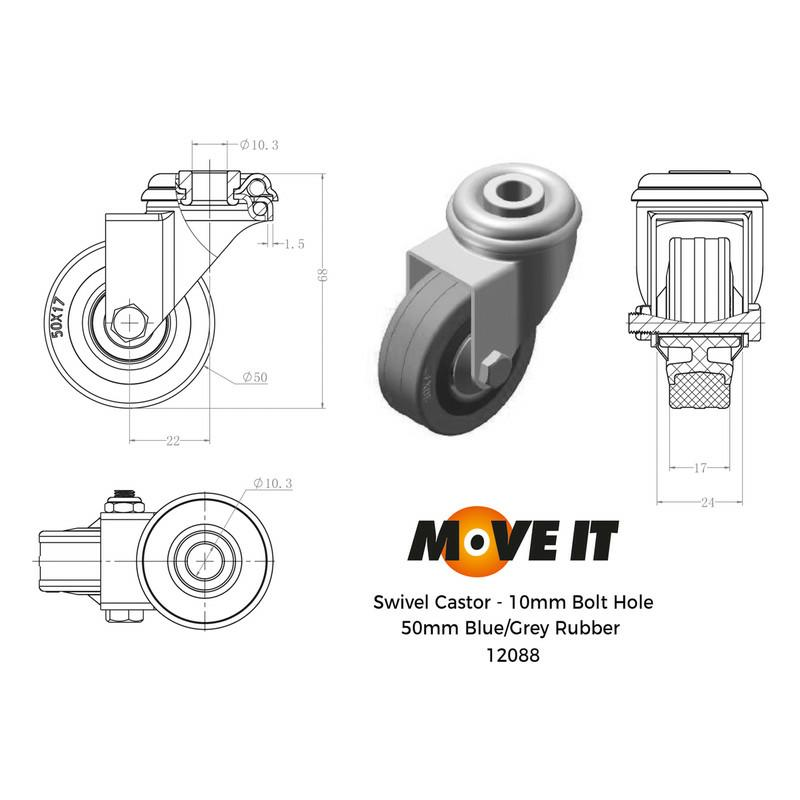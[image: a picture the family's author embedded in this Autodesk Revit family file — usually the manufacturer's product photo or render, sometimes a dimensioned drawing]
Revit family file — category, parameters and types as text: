
# Revit family: ThinkingWall Slatted Screen
name_source: partatom
category: Generic Models
units: mm (PartAtom-declared; Revit-internal decimal feet)

## family parameters
Always vertical = Yes
Can host rebar = No
Cut with Voids When Loaded = No
Maintain Annotation Orientation = No
Part Type = Normal
Room Calculation Point = No
Round Connector Dimension = Use Diameter
Shared = No
Work Plane-Based = No

## types (3) — shared parameters
Description = Mobile slatted office divider to screen work zones flexibly. Part of the ThinkingWall® range for flexible breakout and meeting spaces.
Manufacturer = Logovisual LTD
Model = ThinkingWall® Slatted Screen
Timber Slat = Timber Finish
URL = https://www.logovisual.com
zero-valued in all types: Default Elevation

## per-type parameters (varying)
| type | Length | No of Slat |
| ThinkingWall® Slatted Screen 800 | 800 mm  [stored 2.62467 ft] | 12 |
| ThinkingWall® Slatted Screen 1200 | 1200 mm | 18 |
| ThinkingWall® Slatted Screen 1500 | 1500 mm  [stored 4.92126 ft] | 22 |

note: [stored X ft] marks values corroborated as IEEE doubles in the binary element streams (Revit-internal decimal feet)

## geometry (parser evidence)
native form markers: Sweep x9
no freeform markers — native parametric forms only
